# Revit family: ascot.Vogue Solo 900
name_source: partatom
category: Generic Models
revit_build: Autodesk Revit 2017 (Build: 20171027_0315(x64)
units: mm (PartAtom-declared; Revit-internal decimal feet)

## family parameters
Always vertical = Yes
Can host rebar = No
Cut with Voids When Loaded = No
Part Type = Normal
Room Calculation Point = No
Round Connector Dimension = Use Diameter
Shared = Yes
Work Plane-Based = No

## types (1)
- 2720 x 1200
    Ascot Panel Material = <By Category>
    Description = ASVG 90x60
    Manufacturer = Easycraft Australia Pty Ltd ph 07 3906 7200
    Model = ascot.Vogue Solo 900 (900 x 600)
    Panel_height = 900 mm
    Panel_thickness = 9 mm  [stored 0.0295276 ft]
    Panel_width = 600 mm  [stored 1.9685 ft]
    URL = https://www.easycraft.com.au

note: [stored X ft] marks values corroborated as IEEE doubles in the binary element streams (Revit-internal decimal feet)

## geometry (parser evidence)
native form markers: Blend x2, Sweep x3
no freeform markers — native parametric forms only
